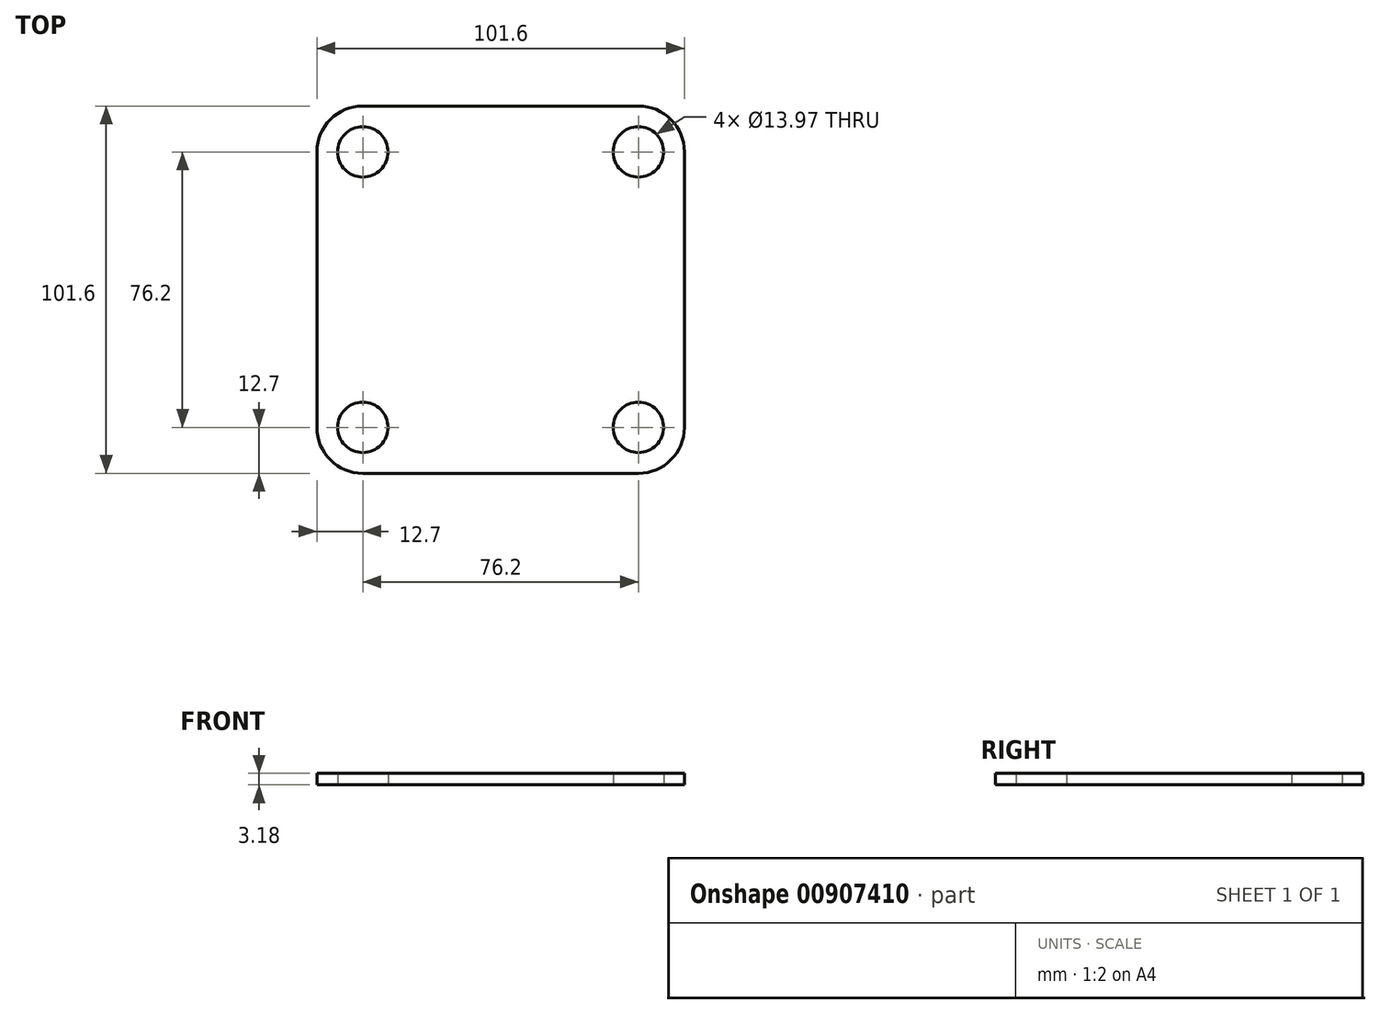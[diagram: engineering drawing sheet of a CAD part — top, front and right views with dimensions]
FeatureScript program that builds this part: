
annotation { "Feature Type Name" : "Feature", "Feature Type Description" : "" }
export const myFeature = defineFeature(function(context is Context, id is Id, definition is map)
    precondition{}
    {
        {
            var Q0;
            Q0=qCreatedBy(makeId("Top.planeOp"),FACE);
            var sketch = newSketch(context, id + "F0", { "sketchPlane" : qUnion([Q0])});
            skCircle(sketch, "E0", {"center": v(0, 76.2) * mm, "radius": 6.99 * mm});
            skCircle(sketch, "E1", {"center": v(76.2, 76.2) * mm, "radius": 6.99 * mm});
            skCircle(sketch, "E2", {"center": v(76.2, 0) * mm, "radius": 6.99 * mm});
            skCircle(sketch, "E3", {"center": v(0, 0) * mm, "radius": 6.99 * mm});
            skLineSegment(sketch, "E4.0", {"start": v(0, 88.9) * mm, "end": v(76.2, 88.9) * mm});
            skLineSegment(sketch, "E4.1", {"start": v(-12.7, 0) * mm, "end": v(-12.7, 76.2) * mm});
            skLineSegment(sketch, "E4.2", {"start": v(0, -12.7) * mm, "end": v(76.2, -12.7) * mm});
            skLineSegment(sketch, "E4.3", {"start": v(88.9, 0) * mm, "end": v(88.9, 76.2) * mm});
            skPoint(sketch, "E5.visualSharp", {"position": v(-12.7, 88.9) * mm});
            skArc(sketch, "E5.filletArc", {"start": v(0, 88.9) * mm, "mid": v(-8.98, 85.18) * mm, "end": v(-12.7, 76.2) * mm});
            skPoint(sketch, "E6.visualSharp", {"position": v(88.9, 88.9) * mm});
            skArc(sketch, "E6.filletArc", {"start": v(88.9, 76.2) * mm, "mid": v(85.18, 85.18) * mm, "end": v(76.2, 88.9) * mm});
            skPoint(sketch, "E7.visualSharp", {"position": v(88.9, -12.7) * mm});
            skArc(sketch, "E7.filletArc", {"start": v(76.2, -12.7) * mm, "mid": v(85.18, -8.98) * mm, "end": v(88.9, 0) * mm});
            skPoint(sketch, "E8.visualSharp", {"position": v(-12.7, -12.7) * mm});
            skArc(sketch, "E8.filletArc", {"start": v(-12.7, 0) * mm, "mid": v(-8.98, -8.98) * mm, "end": v(0, -12.7) * mm});
            skSolve(sketch);
        }
        {
            var Q0;
            Q0 = qSketchRegion(id + "F0", true);
            extrude(context, id + "F1", {"entities" : qUnion([Q0]), "depth" : 3.17 * mm, "offsetDistance" : 25.4 * mm});
        }
    });
